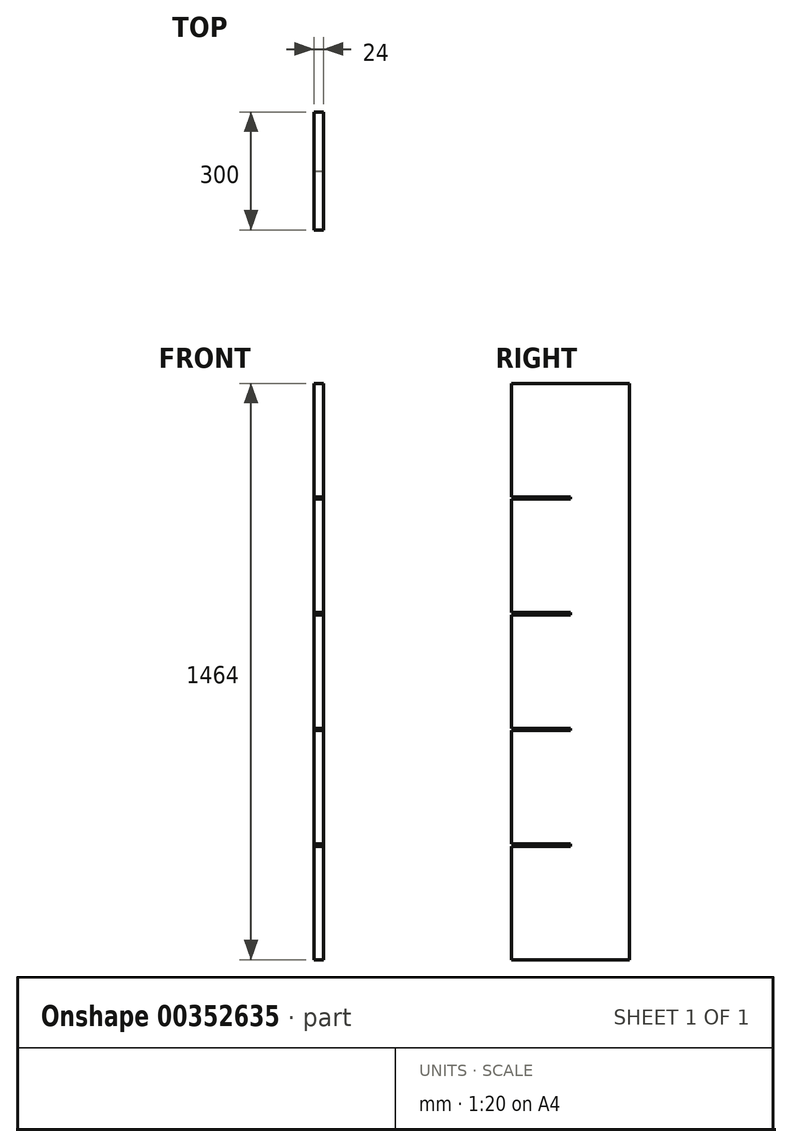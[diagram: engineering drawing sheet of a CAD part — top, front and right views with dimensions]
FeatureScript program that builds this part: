
annotation { "Feature Type Name" : "Feature", "Feature Type Description" : "" }
export const myFeature = defineFeature(function(context is Context, id is Id, definition is map)
    precondition{}
    {
        {
            var Q0;
            Q0=qCreatedBy(makeId("Front.planeOp"),FACE);
            var sketch = newSketch(context, id + "F0", { "sketchPlane" : qUnion([Q0])});
            skLineSegment(sketch, "E0", {"start": v(-117.17, 731.58) * mm, "end": v(-117.17, -732.42) * mm});
            skLineSegment(sketch, "E1", {"start": v(-117.17, -732.42) * mm, "end": v(-93.17, -732.42) * mm});
            skLineSegment(sketch, "E2", {"start": v(-117.17, 731.58) * mm, "end": v(-93.17, 731.58) * mm});
            skLineSegment(sketch, "E3", {"start": v(-93.17, 731.58) * mm, "end": v(-93.17, -732.42) * mm});
            skPoint(sketch, "E4.MirrorCS.end.orphan", {"position": v(-20.62, 182.4) * mm});
            skSolve(sketch);
        }
        {
            var Q0;
            Q0=qSketchRegion(id+"F0",true);
            extrude(context, id + "F1", {"entities" : qUnion([Q0]), "depth" : 300 * mm});
        }
        {
            var Q0;
            Q0=makeQuery(id+"F1.opExtrude","SWEPT_FACE",FACE,{"disambiguationData":[OSD([sQuery(id+"F0.wireOp",EDGE,"E3")])]});
            var sketch = newSketch(context, id + "F2", { "sketchPlane" : qUnion([Q0])});
            skLineSegment(sketch, "E5", {"start": v(-300, 443.58) * mm, "end": v(0, 443.58) * mm});
            skLineSegment(sketch, "E6", {"start": v(-300, 149.58) * mm, "end": v(0, 149.58) * mm});
            skLineSegment(sketch, "E7", {"start": v(-300, 143.58) * mm, "end": v(0, 143.58) * mm});
            skLineSegment(sketch, "E8", {"start": v(-300, -144.42) * mm, "end": v(0, -144.42) * mm});
            skLineSegment(sketch, "E9", {"start": v(-300, -150.42) * mm, "end": v(0, -150.42) * mm});
            skLineSegment(sketch, "E10", {"start": v(-300, -438.42) * mm, "end": v(0, -438.42) * mm});
            skLineSegment(sketch, "E11", {"start": v(-300, -444.42) * mm, "end": v(0, -444.42) * mm});
            skLineSegment(sketch, "E12", {"start": v(-300, 731.58) * mm, "end": v(0, 731.58) * mm});
            skLineSegment(sketch, "E13", {"start": v(-300, -732.42) * mm, "end": v(0, -732.42) * mm});
            skLineSegment(sketch, "E14", {"start": v(-150, 731.58) * mm, "end": v(-150, -732.42) * mm});
            skLineSegment(sketch, "E15", {"start": v(-300, 437.58) * mm, "end": v(0, 437.58) * mm});
            skSolve(sketch);
        }
        {
            var Q0;
            {var subQ0=sQuery(id+"F2.wireOp",EDGE,"E5");var subQ1=makeQuery(id+"F1.opExtrude","CAP_EDGE",EDGE,{"disambiguationData":[OSD([sQuery(id+"F0.wireOp",EDGE,"E3")])],"isStart":false});var subQ2=makeQuery(id+"F2.imprint","INTERSECT",VERTEX,{"derivedFrom":[subQ1,subQ0]});Q0=makeQuery(id+"F2.imprint","IMPRINT",FACE,{"disambiguationData":[TD([[makeQuery(id+"F2.imprint","IMPRINT",EDGE,{"disambiguationData":[TD([[subQ2,-1.0]])],"derivedFrom":subQ0}),-1.0]])]});}
            var Q1;
            {var subQ0=sQuery(id+"F2.wireOp",EDGE,"E6");var subQ1=makeQuery(id+"F1.opExtrude","CAP_EDGE",EDGE,{"disambiguationData":[OSD([sQuery(id+"F0.wireOp",EDGE,"E3")])],"isStart":false});var subQ2=makeQuery(id+"F2.imprint","INTERSECT",VERTEX,{"derivedFrom":[subQ1,subQ0]});Q1=makeQuery(id+"F2.imprint","IMPRINT",FACE,{"disambiguationData":[TD([[makeQuery(id+"F2.imprint","IMPRINT",EDGE,{"disambiguationData":[TD([[subQ2,-1.0]])],"derivedFrom":subQ0}),-1.0]])]});}
            var Q2;
            {var subQ0=sQuery(id+"F2.wireOp",EDGE,"E8");var subQ1=makeQuery(id+"F1.opExtrude","CAP_EDGE",EDGE,{"disambiguationData":[OSD([sQuery(id+"F0.wireOp",EDGE,"E3")])],"isStart":false});var subQ2=makeQuery(id+"F2.imprint","INTERSECT",VERTEX,{"derivedFrom":[subQ1,subQ0]});Q2=makeQuery(id+"F2.imprint","IMPRINT",FACE,{"disambiguationData":[TD([[makeQuery(id+"F2.imprint","IMPRINT",EDGE,{"disambiguationData":[TD([[subQ2,-1.0]])],"derivedFrom":subQ0}),-1.0]])]});}
            var Q3;
            {var subQ0=sQuery(id+"F2.wireOp",EDGE,"E10");var subQ1=makeQuery(id+"F1.opExtrude","CAP_EDGE",EDGE,{"disambiguationData":[OSD([sQuery(id+"F0.wireOp",EDGE,"E3")])],"isStart":false});var subQ2=makeQuery(id+"F2.imprint","INTERSECT",VERTEX,{"derivedFrom":[subQ1,subQ0]});Q3=makeQuery(id+"F2.imprint","IMPRINT",FACE,{"disambiguationData":[TD([[makeQuery(id+"F2.imprint","IMPRINT",EDGE,{"disambiguationData":[TD([[subQ2,-1.0]])],"derivedFrom":subQ0}),-1.0]])]});}
            extrude(context, id + "F3", {"entities" : qUnion([Q0, Q1, Q2, Q3]), "operationType" : NewBodyOperationType.REMOVE, "oppositeDirection" : true, "depth" : 25 * mm});
        }
    });
